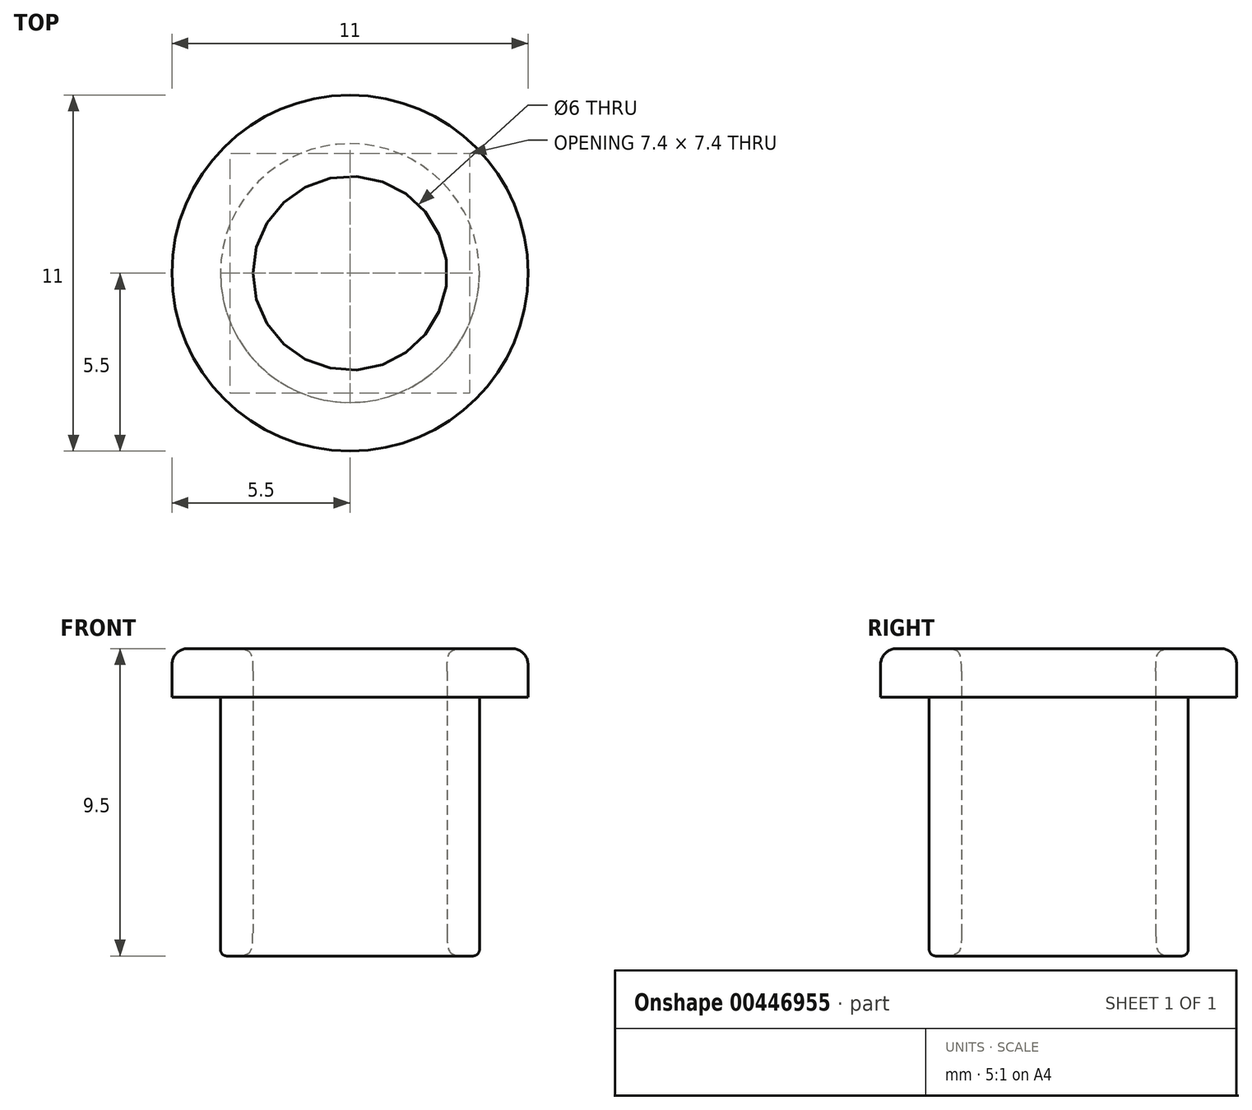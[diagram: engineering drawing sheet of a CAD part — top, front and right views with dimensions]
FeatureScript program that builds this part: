
annotation { "Feature Type Name" : "Feature", "Feature Type Description" : "" }
export const myFeature = defineFeature(function(context is Context, id is Id, definition is map)
    precondition{}
    {
        {
            var Q0;
            Q0=qCreatedBy(makeId("Front.planeOp"),FACE);
            var sketch = newSketch(context, id + "F0", { "sketchPlane" : qUnion([Q0])});
            skLineSegment(sketch, "E0", {"start": v(0, 0) * mm, "end": v(0, 9.5) * mm});
            skLineSegment(sketch, "E1", {"start": v(0, 9.5) * mm, "end": v(2.5, 9.5) * mm});
            skLineSegment(sketch, "E2", {"start": v(2.5, 9.5) * mm, "end": v(2.5, 8) * mm});
            skLineSegment(sketch, "E3", {"start": v(2.5, 8) * mm, "end": v(1, 8) * mm});
            skLineSegment(sketch, "E4", {"start": v(1, 8) * mm, "end": v(1, 0) * mm});
            skLineSegment(sketch, "E5", {"start": v(1, 0) * mm, "end": v(0, 0) * mm});
            skSolve(sketch);
        }
        {
            var Q0;
            Q0=qCreatedBy(makeId("Top.planeOp"),FACE);
            var sketch = newSketch(context, id + "F1", { "sketchPlane" : qUnion([Q0])});
            skCircle(sketch, "E6", {"center": v(-3, 0) * mm, "radius": 3 * mm});
            skSolve(sketch);
        }
        {
            var Q0;
            Q0=makeQuery(id+"F0.imprint","IMPRINT",FACE,{"disambiguationData":[TD([[makeQuery(id+"F0.imprint","IMPRINT",EDGE,{"derivedFrom":sQuery(id+"F0.wireOp",EDGE,"E0")}),-1.0]])]});
            var Q1;
            Q1=sQuery(id+"F1.wireOp",EDGE,"E6");
            revolve(context, id + "F2", {"entities" : qUnion([Q0]), "axis" : qUnion([Q1]), "revolveType" : RevolveType.FULL});
        }
        {
            var Q0;
            Q0=makeQuery(id+"F2.opRevolve","SWEPT_EDGE",EDGE,{"disambiguationData":[OSD([sQuery(id+"F0.wireOp",EDGE,"E0"),sQuery(id+"F0.wireOp",EDGE,"E1")])]});
            var Q1;
            Q1=makeQuery(id+"F2.opRevolve","SWEPT_EDGE",EDGE,{"disambiguationData":[OSD([sQuery(id+"F0.wireOp",EDGE,"E0"),sQuery(id+"F0.wireOp",EDGE,"E5")])]});
            fillet(context, id + "F3", {"entities" : qUnion([Q0, Q1]), "radius" : 0.7 * mm, "tangentPropagation" : true, "rho" : 0.7, "crossSection" : FilletCrossSection.CONIC, "allowEdgeOverflow" : false});
        }
        {
            var Q0;
            Q0=makeQuery(id+"F2.opRevolve","SWEPT_EDGE",EDGE,{"disambiguationData":[OSD([sQuery(id+"F0.wireOp",EDGE,"E4"),sQuery(id+"F0.wireOp",EDGE,"E5")])]});
            fillet(context, id + "F4", {"entities" : qUnion([Q0]), "radius" : 0.2 * mm, "tangentPropagation" : true, "allowEdgeOverflow" : false});
        }
        {
            var Q0;
            Q0=makeQuery(id+"F2.opRevolve","SWEPT_EDGE",EDGE,{"disambiguationData":[OSD([sQuery(id+"F0.wireOp",EDGE,"E1"),sQuery(id+"F0.wireOp",EDGE,"E2")])]});
            fillet(context, id + "F5", {"entities" : qUnion([Q0]), "radius" : 0.5 * mm, "tangentPropagation" : true, "allowEdgeOverflow" : false});
        }
    });
